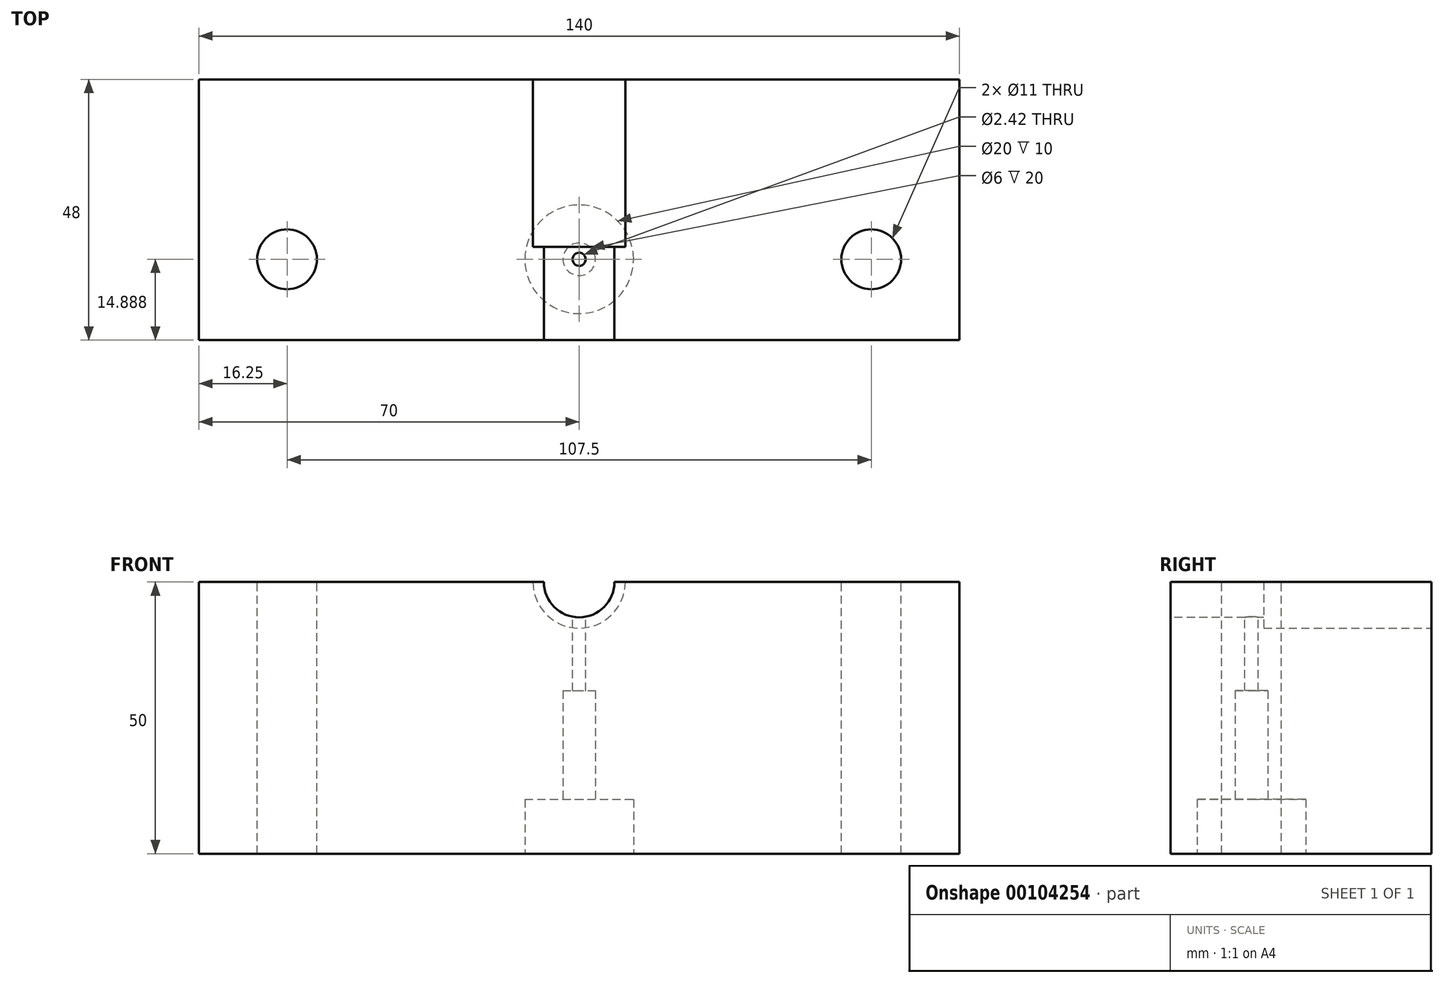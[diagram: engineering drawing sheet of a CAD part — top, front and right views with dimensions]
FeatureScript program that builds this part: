
annotation { "Feature Type Name" : "Feature", "Feature Type Description" : "" }
export const myFeature = defineFeature(function(context is Context, id is Id, definition is map)
    precondition{}
    {
        {
            var Q0;
            Q0=qCreatedBy(makeId("Front.planeOp"),FACE);
            var sketch = newSketch(context, id + "F0", { "sketchPlane" : qUnion([Q0])});
            skLineSegment(sketch, "E0.bottom", {"start": v(0, 0) * mm, "end": v(-140, 0) * mm});
            skLineSegment(sketch, "E0.top", {"start": v(0, 50) * mm, "end": v(-63.5, 50) * mm});
            skLineSegment(sketch, "E0.left", {"start": v(0, 0) * mm, "end": v(0, 50) * mm});
            skLineSegment(sketch, "E0.right", {"start": v(-140, 0) * mm, "end": v(-140, 50) * mm});
            skLineSegment(sketch, "E1.trimOffspring", {"start": v(-76.5, 50) * mm, "end": v(-140, 50) * mm});
            skPoint(sketch, "E2.center.orphan", {"position": v(-70, 50) * mm});
            skLineSegment(sketch, "E3", {"start": v(-63.5, 50) * mm, "end": v(-76.5, 50) * mm});
            skSolve(sketch);
        }
        {
            var Q0;
            Q0=makeQuery(id+"F0.imprint","IMPRINT",FACE,{"disambiguationData":[TD([[makeQuery(id+"F0.imprint","IMPRINT",EDGE,{"derivedFrom":sQuery(id+"F0.wireOp",EDGE,"E0.bottom")}),-1.0]])]});
            extrude(context, id + "F1", {"entities" : qUnion([Q0]), "depth" : 48 * mm});
        }
        {
            var Q0;
            Q0=makeQuery(id+"F1.opExtrude","SWEPT_FACE",FACE,{"disambiguationData":[OSD([sQuery(id+"F0.wireOp",EDGE,"E1.trimOffspring")])]});
            var sketch = newSketch(context, id + "F2", { "sketchPlane" : qUnion([Q0])});
            skCircle(sketch, "E4", {"center": v(-123.75, -33.11) * mm, "radius": 5.5 * mm});
            skCircle(sketch, "E5", {"center": v(-16.25, -33.11) * mm, "radius": 5.5 * mm});
            skSolve(sketch);
        }
        {
            var Q0;
            Q0=qSketchRegion(id+"F2",true);
            extrude(context, id + "F3", {"entities" : qUnion([Q0]), "operationType" : NewBodyOperationType.REMOVE, "endBound" : BoundingType.THROUGH_ALL, "oppositeDirection" : true, "depth" : 25 * mm});
        }
        {
            var Q0;
            Q0=makeQuery(id+"F1.opExtrude","CAP_FACE",FACE,{"disambiguationData":[OSD([sQuery(id+"F0.wireOp",EDGE,"E0.bottom"),sQuery(id+"F0.wireOp",EDGE,"E0.top"),sQuery(id+"F0.wireOp",EDGE,"E0.left"),sQuery(id+"F0.wireOp",EDGE,"E0.right"),sQuery(id+"F0.wireOp",EDGE,"E1.trimOffspring"),sQuery(id+"F0.wireOp",EDGE,"E3")])],"isStart":false});
            var sketch = newSketch(context, id + "F4", { "sketchPlane" : qUnion([Q0])});
            skCircle(sketch, "E6", {"center": v(-70, 50) * mm, "radius": 6.5 * mm});
            skSolve(sketch);
        }
        {
            var Q0;
            Q0=qSketchRegion(id+"F4",true);
            extrude(context, id + "F5", {"entities" : qUnion([Q0]), "operationType" : NewBodyOperationType.REMOVE, "oppositeDirection" : true, "depth" : 20 * mm});
        }
        {
            var Q0;
            Q0=makeQuery(id+"F1.opExtrude","CAP_FACE",FACE,{"disambiguationData":[OSD([sQuery(id+"F0.wireOp",EDGE,"E0.bottom"),sQuery(id+"F0.wireOp",EDGE,"E0.top"),sQuery(id+"F0.wireOp",EDGE,"E0.left"),sQuery(id+"F0.wireOp",EDGE,"E0.right"),sQuery(id+"F0.wireOp",EDGE,"E1.trimOffspring"),sQuery(id+"F0.wireOp",EDGE,"E3")])],"isStart":true});
            var sketch = newSketch(context, id + "F6", { "sketchPlane" : qUnion([Q0])});
            skCircle(sketch, "E7", {"center": v(70, 50) * mm, "radius": 8.5 * mm});
            skSolve(sketch);
        }
        {
            var Q0;
            Q0=qSketchRegion(id+"F6",true);
            extrude(context, id + "F7", {"entities" : qUnion([Q0]), "operationType" : NewBodyOperationType.REMOVE, "oppositeDirection" : true, "depth" : (28 + 2.85) * mm});
        }
        {
            var Q0;
            {var subQ0=sQuery(id+"F0.wireOp",EDGE,"E0.top");var subQ1=sQuery(id+"F0.wireOp",EDGE,"E1.trimOffspring");var subQ2=sQuery(id+"F0.wireOp",EDGE,"E3");var subQ5=sQuery(id+"F0.wireOp",EDGE,"E0.left");Q0=makeQuery(id+"F7.boolean.opBoolean","SPLIT",FACE,{"disambiguationData":[TD([makeQuery(id+"F1.opExtrude","SWEPT_FACE",FACE,{"disambiguationData":[OSD([subQ5])]})])],"derivedFrom":makeQuery(id+"F1.opExtrude","SWEPT_FACE",FACE,{"disambiguationData":[OSD([subQ0,subQ1,subQ2])]})});}
            var sketch = newSketch(context, id + "F8", { "sketchPlane" : qUnion([Q0])});
            skCircle(sketch, "E8", {"center": v(-70, -33.11) * mm, "radius": 1.21 * mm});
            skSolve(sketch);
        }
        {
            var Q0;
            Q0=qSketchRegion(id+"F8",true);
            extrude(context, id + "F9", {"entities" : qUnion([Q0]), "operationType" : NewBodyOperationType.REMOVE, "endBound" : BoundingType.THROUGH_ALL, "oppositeDirection" : true, "depth" : 25 * mm});
        }
        {
            var Q0;
            Q0=makeQuery(id+"F1.opExtrude","SWEPT_FACE",FACE,{"disambiguationData":[OSD([sQuery(id+"F0.wireOp",EDGE,"E0.bottom")])]});
            var sketch = newSketch(context, id + "F10", { "sketchPlane" : qUnion([Q0])});
            skCircle(sketch, "E9", {"center": v(-70, 33.11) * mm, "radius": 10 * mm});
            skSolve(sketch);
        }
        {
            var Q0;
            Q0=qSketchRegion(id+"F10",true);
            extrude(context, id + "F11", {"entities" : qUnion([Q0]), "operationType" : NewBodyOperationType.REMOVE, "oppositeDirection" : true, "depth" : 10 * mm});
        }
        {
            var Q0;
            Q0=makeQuery(id+"F11.boolean.opBoolean","COPY",FACE,{"derivedFrom":makeQuery(id+"F11.opExtrude","CAP_FACE",FACE,{"disambiguationData":[OSD([sQuery(id+"F10.wireOp",EDGE,"E9")])],"isStart":false})});
            var sketch = newSketch(context, id + "F12", { "sketchPlane" : qUnion([Q0])});
            skCircle(sketch, "E10", {"center": v(-70, 33.11) * mm, "radius": 3 * mm});
            skSolve(sketch);
        }
        {
            var Q0;
            Q0 = qSketchRegion(id + "F12", true);
            extrude(context, id + "F13", {"entities" : qUnion([Q0]), "operationType" : NewBodyOperationType.REMOVE, "oppositeDirection" : true, "depth" : 20 * mm});
        }
    });
